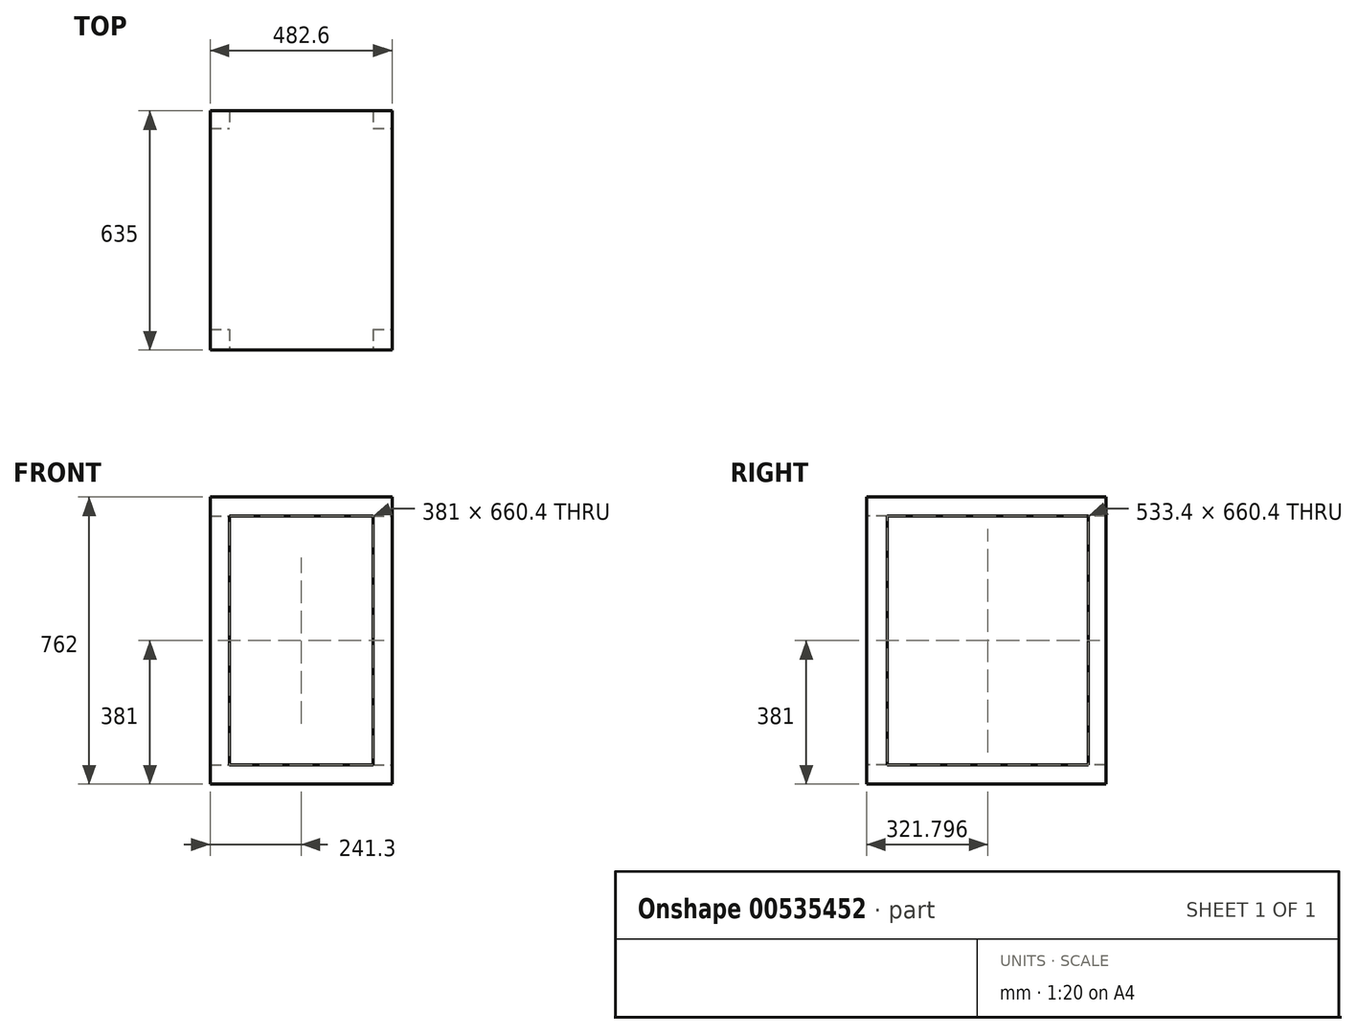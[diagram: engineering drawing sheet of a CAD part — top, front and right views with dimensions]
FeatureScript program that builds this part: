
annotation { "Feature Type Name" : "Feature", "Feature Type Description" : "" }
export const myFeature = defineFeature(function(context is Context, id is Id, definition is map)
    precondition{}
    {
        {
            var Q0;
            Q0=qCreatedBy(makeId("Front.planeOp"),FACE);
            var sketch = newSketch(context, id + "F0", { "sketchPlane" : qUnion([Q0])});
            skLineSegment(sketch, "E0.bottom", {"start": v(-241.3, 381) * mm, "end": v(241.3, 381) * mm});
            skLineSegment(sketch, "E0.top", {"start": v(-241.3, -381) * mm, "end": v(241.3, -381) * mm});
            skLineSegment(sketch, "E0.left", {"start": v(-241.3, 381) * mm, "end": v(-241.3, -381) * mm});
            skLineSegment(sketch, "E0.right", {"start": v(241.3, 381) * mm, "end": v(241.3, -381) * mm});
            skPoint(sketch, "E0.middle", {"position": v(0, 0) * mm});
            skLineSegment(sketch, "E1", {"start": v(-190.5, 381) * mm, "end": v(-190.5, -381) * mm});
            skLineSegment(sketch, "E2", {"start": v(190.5, 381) * mm, "end": v(190.5, -381) * mm});
            skLineSegment(sketch, "E3", {"start": v(-190.5, -330.2) * mm, "end": v(190.5, -330.2) * mm});
            skLineSegment(sketch, "E4", {"start": v(-190.5, 330.2) * mm, "end": v(190.5, 330.2) * mm});
            skSolve(sketch);
        }
        {
            var Q0;
            {var subQ5=sQuery(id+"F0.wireOp",EDGE,"E4");Q0=makeQuery(id+"F0.imprint","IMPRINT",FACE,{"disambiguationData":[TD([[makeQuery(id+"F0.imprint","IMPRINT",EDGE,{"derivedFrom":subQ5}),1.0]])]});}
            var Q1;
            {var subQ4=sQuery(id+"F0.wireOp",EDGE,"E0.right");Q1=makeQuery(id+"F0.imprint","IMPRINT",FACE,{"disambiguationData":[TD([[makeQuery(id+"F0.imprint","IMPRINT",EDGE,{"derivedFrom":subQ4}),-1.0]])]});}
            var Q2;
            {var subQ5=sQuery(id+"F0.wireOp",EDGE,"E3");Q2=makeQuery(id+"F0.imprint","IMPRINT",FACE,{"disambiguationData":[TD([[makeQuery(id+"F0.imprint","IMPRINT",EDGE,{"derivedFrom":subQ5}),-1.0]])]});}
            var Q3;
            {var subQ0=sQuery(id+"F0.wireOp",EDGE,"E0.left");Q3=makeQuery(id+"F0.imprint","IMPRINT",FACE,{"disambiguationData":[TD([[makeQuery(id+"F0.imprint","IMPRINT",EDGE,{"derivedFrom":subQ0}),1.0]])]});}
            var Q4;
            {var subQ0=sQuery(id+"F0.wireOp",EDGE,"OaRCWpEt-IZd2-p90J-ZdkO-JAgXkQZi0FDD.bottom");var subQ1=sQuery(id+"F0.wireOp",EDGE,"E1");var subQ2=makeQuery(id+"F0.imprint","INTERSECT",VERTEX,{"derivedFrom":[subQ1,subQ0]});Q4=makeQuery(id+"F0.imprint","IMPRINT",FACE,{"disambiguationData":[TD([[makeQuery(id+"F0.imprint","IMPRINT",EDGE,{"disambiguationData":[TD([[subQ2,-1.0]])],"derivedFrom":subQ1}),1.0]])]});}
            var Q5;
            {var subQ5=sQuery(id+"F0.wireOp",EDGE,"OaRCWpEt-IZd2-p90J-ZdkO-JAgXkQZi0FDD.left");Q5=makeQuery(id+"F0.imprint","IMPRINT",FACE,{"disambiguationData":[TD([[makeQuery(id+"F0.imprint","IMPRINT",EDGE,{"derivedFrom":subQ5}),1.0]])]});}
            var Q6;
            {var subQ5=sQuery(id+"F0.wireOp",EDGE,"OaRCWpEt-IZd2-p90J-ZdkO-JAgXkQZi0FDD.right");Q6=makeQuery(id+"F0.imprint","IMPRINT",FACE,{"disambiguationData":[TD([[makeQuery(id+"F0.imprint","IMPRINT",EDGE,{"derivedFrom":subQ5}),-1.0]])]});}
            extrude(context, id + "F1", {"entities" : qUnion([Q0, Q1, Q2, Q3, Q4, Q5, Q6]), "oppositeDirection" : true, "depth" : 635 * mm, "offsetDistance" : 25.4 * mm});
        }
        {
            var Q0;
            Q0=makeQuery(id+"F1.opExtrude","SWEPT_FACE",FACE,{"disambiguationData":[OSD([sQuery(id+"F0.wireOp",EDGE,"E0.right")])]});
            var sketch = newSketch(context, id + "F2", { "sketchPlane" : qUnion([Q0])});
            skLineSegment(sketch, "E5.bottom", {"start": v(55.1, 330.2) * mm, "end": v(588.5, 330.2) * mm});
            skLineSegment(sketch, "E5.top", {"start": v(55.1, -330.2) * mm, "end": v(588.5, -330.2) * mm});
            skLineSegment(sketch, "E5.left", {"start": v(55.1, 330.2) * mm, "end": v(55.1, -330.2) * mm});
            skLineSegment(sketch, "E5.right", {"start": v(588.5, 330.2) * mm, "end": v(588.5, -330.2) * mm});
            skSolve(sketch);
        }
        {
            var Q0;
            Q0=makeQuery(id+"F2.imprint","IMPRINT",FACE,{"disambiguationData":[TD([[makeQuery(id+"F2.imprint","IMPRINT",EDGE,{"derivedFrom":sQuery(id+"F2.wireOp",EDGE,"E5.bottom")}),-1.0]])]});
            var Q1;
            {var subQ0=sQuery(id+"F2.wireOp",EDGE,"E5.top");Q1=makeQuery(id+"F2.imprint","IMPRINT",FACE,{"disambiguationData":[TD([[makeQuery(id+"F2.imprint","IMPRINT",EDGE,{"derivedFrom":subQ0}),1.0]])]});}
            extrude(context, id + "F3", {"entities" : qUnion([Q0, Q1]), "operationType" : NewBodyOperationType.REMOVE, "endBound" : BoundingType.THROUGH_ALL, "oppositeDirection" : true, "depth" : 50.8 * mm, "offsetDistance" : 25.4 * mm});
        }
        {
            var Q0;
            {var subQ0=sQuery(id+"F0.wireOp",EDGE,"E3");Q0=makeQuery(id+"F0.imprint","IMPRINT",FACE,{"disambiguationData":[TD([[makeQuery(id+"F0.imprint","IMPRINT",EDGE,{"derivedFrom":subQ0}),1.0]])]});}
            extrude(context, id + "F4", {"entities" : qUnion([Q0]), "operationType" : NewBodyOperationType.REMOVE, "endBound" : BoundingType.THROUGH_ALL, "oppositeDirection" : true, "depth" : 25.4 * mm, "offsetDistance" : 25.4 * mm});
        }
    });
